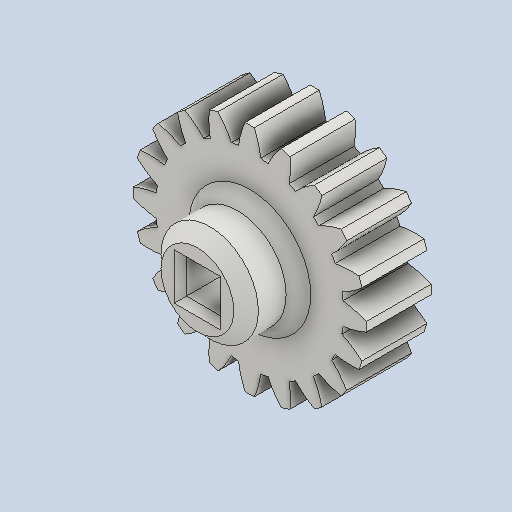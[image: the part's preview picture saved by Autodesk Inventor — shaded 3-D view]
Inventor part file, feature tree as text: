
AUTODESK INVENTOR PART (.ipt)
format: ipt  version: 2022 (Build 260153000, 153)  size: 303,104 bytes
history: native  units: in
note: dims shown in document units (in); Inventor stores cm internally (conversion verified against a paired STEP export)
features: other x12, sketch x4, plane x3
ambient origin geometry x8: Origin, YZ Plane, XZ Plane, XY Plane, X Axis, Y Axis, Z Axis, Center Point
bodies: Solid1 (feature_tree)
feature tree (19):
  other  "Spur Gear2"
  other  "Solid1::Spur Gear2"
  other  "TaggingFeature1"
  sketch  "Sketch1"  dims[d0=0.3937in]
  sketch  "Sketch2"  dims[d9=0.0in]
  sketch  "Sketch3"  dims[d14=0.0in]
  sketch  "Sketch4"  dims[d15=1.0in d16=0.0in d17=0.0in d18=0.0in d19=1.0in]
  plane  "XZ Plane_1"
  plane  "Work Plane2"
  plane  "Work Plane3"
  other  "Srf1"
  other  "Srf1::Derived"
  other  "Start plane iMate"
  other  "Distance iMate"
  other  "Position iMate"
  other  "Mesh iMate"
  other  "Axis iMate"
  other  "Mesh iMate2"
  other  "Align iMate"
